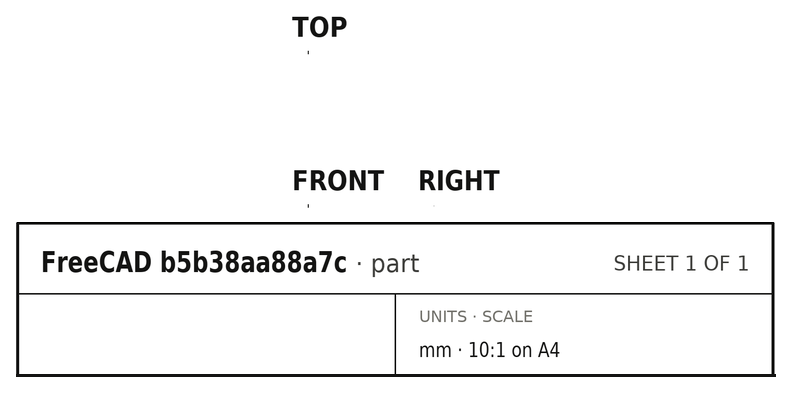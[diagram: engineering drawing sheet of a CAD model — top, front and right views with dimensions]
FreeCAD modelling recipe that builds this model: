
FCSTD DOCUMENT  (FreeCAD 0.21R33694 (Git))
Label: Lee_microstrip
License: All rights reserved
LicenseURL: http://en.wikipedia.org/wiki/All_rights_reserved
objects: Part::Part2DObjectPython×4, Part::Cut×1, Part::FeaturePython×1, App::FeaturePython×1
note: 6 computed .brp shape members not serialized (recipe doc carries the construction recipe); baked Part::Feature solids carry a one-line shape summary decoded from their .brp

FEATURE [Part::Part2DObjectPython] Line  label="_PV1"  # Draft 2D object (typed FeaturePython)
  Area = 0
  ChamferSize = 0
  Closed = false
  End = (0.00125,0.00025,0)
  FilletRadius = 0
  Length = 0.00025
  MakeFace = true
  Placement = pos=(0.0025,0,0) rot=(0,0,1;0rad)
  Points = (2) [(-0.00125,3.82702e-20,0),(-0.00125,0.00025,0)]
  Start = (0.00125,0,0)
  Subdivisions = 0
FEATURE [Part::Part2DObjectPython] Rectangle004  label="Lee_semiconductor"  # Draft 2D object (typed FeaturePython)
  Area = 6.25e-07
  ChamferSize = 0
  Columns = 1
  FilletRadius = 0
  Height = 0.00025
  Length = 0.0025
  MakeFace = true
  Rows = 1
FEATURE [Part::Part2DObjectPython] Rectangle005  label="strip001"  # Draft 2D object (typed FeaturePython)
  Area = 1.25e-08
  ChamferSize = 0
  Columns = 1
  FilletRadius = 0
  Height = 5e-05
  Length = 0.00025
  MakeFace = true
  Placement = pos=(0.001125,0.00025,0) rot=(0,0,1;0rad)
  Rows = 1
FEATURE [Part::Part2DObjectPython] Rectangle006  label="air001"  # Draft 2D object (typed FeaturePython)
  Area = 5.625e-06
  ChamferSize = 0
  Columns = 1
  FilletRadius = 0
  Height = 0.00225
  Length = 0.0025
  MakeFace = true
  Placement = pos=(0,0.00025,0) rot=(0,0,1;0rad)
  Rows = 1
FEATURE [Part::Cut] Cut001  label="air002"
  Base = -> Rectangle006
  Tool = -> Rectangle005
FEATURE [Part::FeaturePython] BooleanFragments001  label="Lee_microstrip"  # WARN: FeaturePython — macro-defined, semantics opaque (R4)
  Mode = 0
  Objects = -> [Rectangle004,Cut001]
  Tolerance = 0
FEATURE [App::FeaturePython] Text  label="_M1(voltage){V1}"  # WARN: FeaturePython — macro-defined, semantics opaque (R4)
  Placement = pos=(0.00123975,-0.000526531,0) rot=(0,0,1;0rad)
  Text = .
